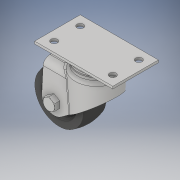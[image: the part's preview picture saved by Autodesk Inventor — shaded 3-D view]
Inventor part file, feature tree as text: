
AUTODESK INVENTOR PART (.ipt)
format: ipt  version: 2018.2 (Build 222227000, 227)  size: 368,128 bytes
history: native  units: in
note: dims shown in document units (in); Inventor stores cm internally (conversion verified against a paired STEP export)
features: revolve x1, boolean_combine x1
ambient origin geometry x8: Origin, YZ Plane, XZ Plane, XY Plane, X Axis, Y Axis, Z Axis, Center Point
bodies: Solid1 (feature_tree), Solid2 (feature_tree)
feature tree (2):
  revolve  "Revolve1"  [1 undecoded]
  boolean_combine  "Combine2"
note: 1 required parameter value undecoded (feature->parameter linkage not recoverable at this tier; creation-order binding heuristic only, values carry confidence <= 0.55)
